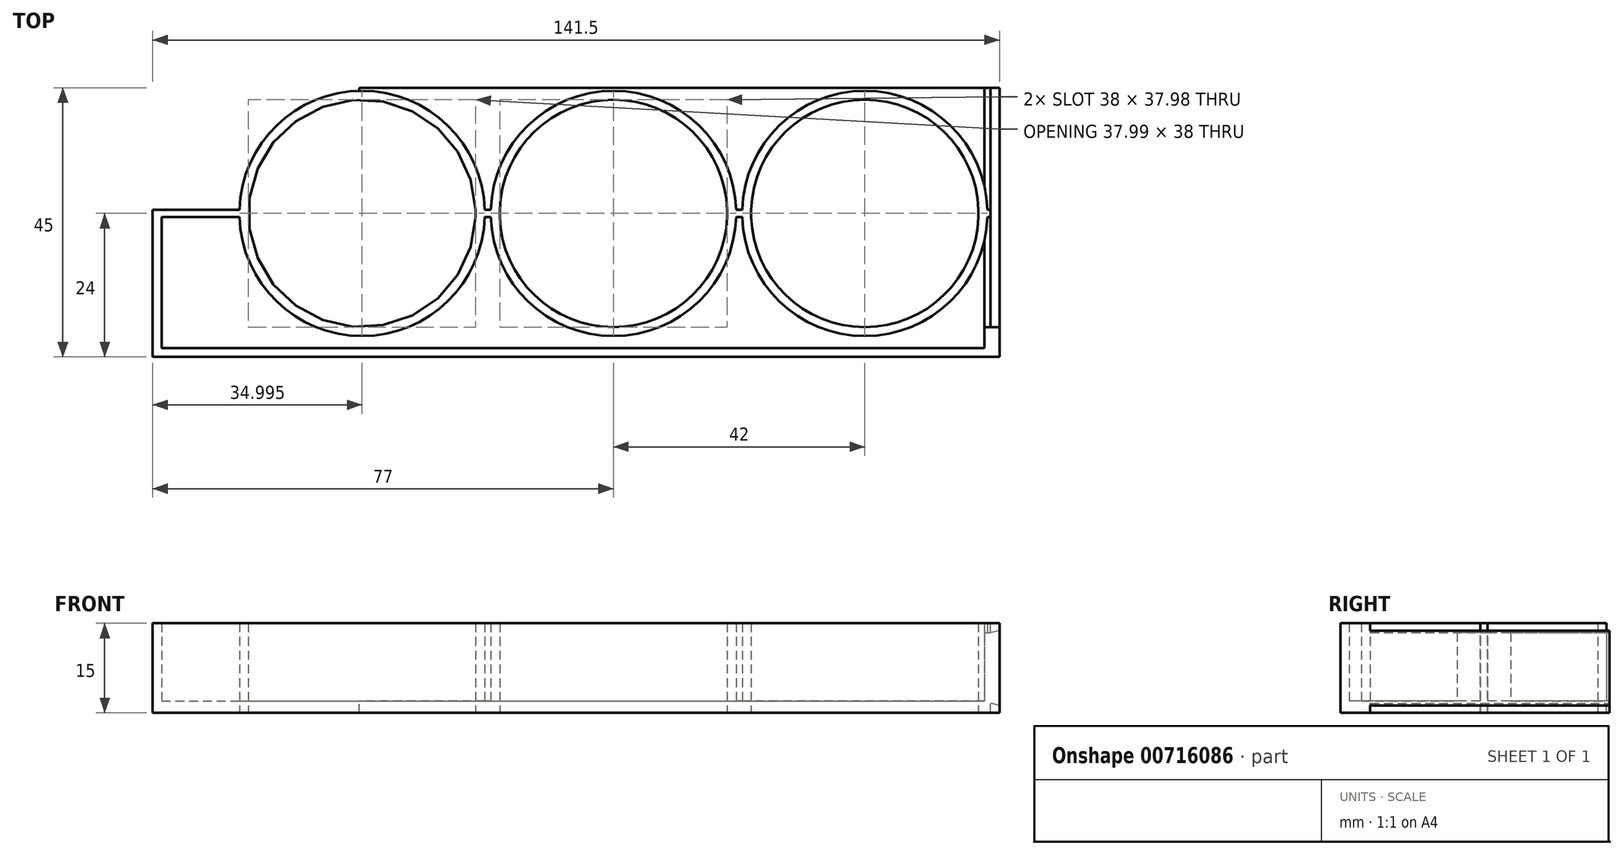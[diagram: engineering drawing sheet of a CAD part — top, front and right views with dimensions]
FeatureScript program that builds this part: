
annotation { "Feature Type Name" : "Feature", "Feature Type Description" : "" }
export const myFeature = defineFeature(function(context is Context, id is Id, definition is map)
    precondition{}
    {
        {
            var Q0;
            Q0=qCreatedBy(makeId("Top.planeOp"),FACE);
            var sketch = newSketch(context, id + "F0", { "sketchPlane" : qUnion([Q0])});
            skCircle(sketch, "E0", {"center": v(-41.38, 6.47) * mm, "radius": 19 * mm});
            skCircle(sketch, "E1.1.0.0", {"center": v(0.62, 6.47) * mm, "radius": 19 * mm});
            skCircle(sketch, "E1.2.0.0", {"center": v(42.62, 6.47) * mm, "radius": 19 * mm});
            skLineSegment(sketch, "E1.direction1", {"start": v(-41.38, 6.47) * mm, "end": v(0.62, 6.47) * mm, "construction": true});
            skLineSegment(sketch, "E2.bottom", {"start": v(-74.88, 27.47) * mm, "end": v(63.62, 27.47) * mm});
            skLineSegment(sketch, "E2.top", {"start": v(-74.88, -16.03) * mm, "end": v(63.62, -16.03) * mm});
            skLineSegment(sketch, "E2.left", {"start": v(-74.88, 27.47) * mm, "end": v(-74.88, -16.03) * mm});
            skLineSegment(sketch, "E2.right", {"start": v(63.62, 27.47) * mm, "end": v(63.62, -16.03) * mm});
            skCircle(sketch, "E3", {"center": v(-41.38, 6.47) * mm, "radius": 20.5 * mm});
            skCircle(sketch, "E4", {"center": v(0.62, 6.47) * mm, "radius": 20.5 * mm});
            skCircle(sketch, "E5", {"center": v(42.62, 6.47) * mm, "radius": 20.5 * mm});
            skLineSegment(sketch, "E6.0", {"start": v(65.12, 27.47) * mm, "end": v(65.12, -17.53) * mm});
            skLineSegment(sketch, "E6.1", {"start": v(-76.38, -17.53) * mm, "end": v(65.12, -17.53) * mm});
            skLineSegment(sketch, "E6.2", {"start": v(-76.38, 27.47) * mm, "end": v(-76.38, -17.53) * mm});
            skLineSegment(sketch, "E7", {"start": v(63.62, 27.47) * mm, "end": v(65.12, 27.47) * mm});
            skLineSegment(sketch, "E8", {"start": v(-76.38, 27.47) * mm, "end": v(-74.88, 27.47) * mm});
            skSolve(sketch);
        }
        {
            var Q0;
            Q0=makeQuery(id+"F0.imprint","IMPRINT",FACE,{"disambiguationData":[TD([[makeQuery(id+"F0.imprint","IMPRINT",EDGE,{"derivedFrom":sQuery(id+"F0.wireOp",EDGE,"E0")}),-1.0]])]});
            var Q1;
            Q1=makeQuery(id+"F0.imprint","IMPRINT",FACE,{"disambiguationData":[TD([[makeQuery(id+"F0.imprint","IMPRINT",EDGE,{"derivedFrom":sQuery(id+"F0.wireOp",EDGE,"E1.1.0.0")}),-1.0]])]});
            var Q2;
            Q2=makeQuery(id+"F0.imprint","IMPRINT",FACE,{"disambiguationData":[TD([[makeQuery(id+"F0.imprint","IMPRINT",EDGE,{"derivedFrom":sQuery(id+"F0.wireOp",EDGE,"E1.2.0.0")}),-1.0]])]});
            var Q3;
            Q3=makeQuery(id+"F0.imprint","IMPRINT",FACE,{"disambiguationData":[TD([[makeQuery(id+"F0.imprint","IMPRINT",EDGE,{"derivedFrom":sQuery(id+"F0.wireOp",EDGE,"E2.top")}),-1.0]])]});
            extrude(context, id + "F1", {"entities" : qUnion([Q0, Q1, Q2, Q3]), "depth" : 15 * mm, "offsetDistance" : 25 * mm});
        }
        {
            var Q0;
            Q0=makeQuery(id+"F0.imprint","IMPRINT",FACE,{"disambiguationData":[TD([[makeQuery(id+"F0.imprint","IMPRINT",EDGE,{"derivedFrom":sQuery(id+"F0.wireOp",EDGE,"E2.bottom")}),-1.0]])]});
            extrude(context, id + "F2", {"entities" : qUnion([Q0]), "depth" : 2 * mm, "offsetDistance" : 25 * mm});
        }
        {
            var Q0;
            Q0=makeQuery(id+"F1.opExtrude","SWEPT_BODY",BODY,{"disambiguationData":[OSD([sQuery(id+"F0.wireOp",EDGE,"E1.1.0.0"),sQuery(id+"F0.wireOp",EDGE,"E4")])]});
            var Q1;
            Q1=makeQuery(id+"F1.opExtrude","SWEPT_BODY",BODY,{"disambiguationData":[OSD([sQuery(id+"F0.wireOp",EDGE,"E1.2.0.0"),sQuery(id+"F0.wireOp",EDGE,"E5")])]});
            var Q2;
            Q2=makeQuery(id+"F1.opExtrude","SWEPT_BODY",BODY,{"disambiguationData":[OSD([sQuery(id+"F0.wireOp",EDGE,"E2.top"),sQuery(id+"F0.wireOp",EDGE,"E2.left"),sQuery(id+"F0.wireOp",EDGE,"E2.right"),sQuery(id+"F0.wireOp",EDGE,"E6.0"),sQuery(id+"F0.wireOp",EDGE,"E6.1"),sQuery(id+"F0.wireOp",EDGE,"E6.2"),sQuery(id+"F0.wireOp",EDGE,"E7"),sQuery(id+"F0.wireOp",EDGE,"E8")])]});
            var Q3;
            Q3=makeQuery(id+"F2.opExtrude","SWEPT_BODY",BODY,{"disambiguationData":[OSD([sQuery(id+"F0.wireOp",EDGE,"E2.bottom"),sQuery(id+"F0.wireOp",EDGE,"E2.top"),sQuery(id+"F0.wireOp",EDGE,"E2.left"),sQuery(id+"F0.wireOp",EDGE,"E2.right"),sQuery(id+"F0.wireOp",EDGE,"E3"),sQuery(id+"F0.wireOp",EDGE,"E4"),sQuery(id+"F0.wireOp",EDGE,"E5")])]});
            var Q4;
            Q4=makeQuery(id+"F1.opExtrude","SWEPT_BODY",BODY,{"disambiguationData":[OSD([sQuery(id+"F0.wireOp",EDGE,"E0"),sQuery(id+"F0.wireOp",EDGE,"E3")])]});
            booleanBodies(context, id + "F3", {"operationType" : BooleanOperationType.UNION, "tools" : qUnion([Q0, Q1, Q2, Q3, Q4])});
        }
        {
            var Q0;
            Q0=makeQuery(id+"F1.opExtrude","SWEPT_BODY",BODY,{"disambiguationData":[OSD([sQuery(id+"F0.wireOp",EDGE,"E1.1.0.0"),sQuery(id+"F0.wireOp",EDGE,"E4")])]});
            var Q1;
            Q1=sQuery(id+"F0.wireOp",VERTEX,"E1.direction1.end");
            var Q2;
            Q2=qCreatedBy(makeId("Origin.pointOp"),VERTEX);
            transform(context, id + "F4", {"entities" : qUnion([Q0]), "transformType" : TransformType.TRANSLATION_ENTITY, "oppositeDirectionEntity" : false, "transformLine" : qUnion([Q1, Q2]), "makeCopy" : false});
        }
        {
            var Q0;
            Q0=makeQuery(id+"F1.opExtrude","SWEPT_FACE",FACE,{"disambiguationData":[OSD([sQuery(id+"F0.wireOp",EDGE,"E6.2")])]});
            var sketch = newSketch(context, id + "F5", { "sketchPlane" : qUnion([Q0])});
            skLineSegment(sketch, "E9.bottom", {"start": v(0.6, 0) * mm, "end": v(-0.6, 0) * mm});
            skLineSegment(sketch, "E9.top", {"start": v(0.6, 15) * mm, "end": v(-0.6, 15) * mm});
            skLineSegment(sketch, "E9.left", {"start": v(0.6, 0) * mm, "end": v(0.6, 15) * mm});
            skLineSegment(sketch, "E9.right", {"start": v(-0.6, 0) * mm, "end": v(-0.6, 15) * mm});
            skSolve(sketch);
        }
        {
            var Q0;
            Q0=makeQuery(id+"F5.imprint","IMPRINT",FACE,{"disambiguationData":[TD([[makeQuery(id+"F5.imprint","IMPRINT",EDGE,{"derivedFrom":sQuery(id+"F5.wireOp",EDGE,"E9.bottom")}),1.0]])]});
            extrude(context, id + "F6", {"entities" : qUnion([Q0]), "operationType" : NewBodyOperationType.ADD, "oppositeDirection" : true, "depth" : 16 * mm, "offsetDistance" : 25 * mm});
        }
        {
            var Q0;
            Q0=makeQuery(id+"F2.opExtrude","CAP_FACE",FACE,{"disambiguationData":[OSD([sQuery(id+"F0.wireOp",EDGE,"E2.bottom"),sQuery(id+"F0.wireOp",EDGE,"E2.top"),sQuery(id+"F0.wireOp",EDGE,"E2.left"),sQuery(id+"F0.wireOp",EDGE,"E2.right"),sQuery(id+"F0.wireOp",EDGE,"E3"),sQuery(id+"F0.wireOp",EDGE,"E4"),sQuery(id+"F0.wireOp",EDGE,"E5")])],"isStart":false});
            var sketch = newSketch(context, id + "F7", { "sketchPlane" : qUnion([Q0])});
            skLineSegment(sketch, "E10", {"start": v(-42.5, 21) * mm, "end": v(-42.5, 20.5) * mm});
            skSolve(sketch);
        }
        {
            var Q0;
            {var subQ7=sQuery(id+"F7.wireOp",EDGE,"E10");Q0=makeQuery(id+"F7.imprint","IMPRINT",FACE,{"disambiguationData":[TD([[makeQuery(id+"F7.imprint","IMPRINT",EDGE,{"derivedFrom":subQ7}),-1.0]])]});}
            extrude(context, id + "F8", {"entities" : qUnion([Q0]), "operationType" : NewBodyOperationType.REMOVE, "endBound" : BoundingType.THROUGH_ALL, "oppositeDirection" : true, "depth" : 25 * mm, "offsetDistance" : 25 * mm});
        }
        {
            var Q0;
            Q0=makeQuery(id+"F6.boolean.opBoolean","MERGE",FACE,{"derivedFrom":[makeQuery(id+"F1.opExtrude","CAP_FACE",FACE,{"disambiguationData":[OSD([sQuery(id+"F0.wireOp",EDGE,"E0"),sQuery(id+"F0.wireOp",EDGE,"E3")])],"isStart":false}),makeQuery(id+"F1.opExtrude","CAP_FACE",FACE,{"disambiguationData":[OSD([sQuery(id+"F0.wireOp",EDGE,"E2.top"),sQuery(id+"F0.wireOp",EDGE,"E2.left"),sQuery(id+"F0.wireOp",EDGE,"E2.right"),sQuery(id+"F0.wireOp",EDGE,"E6.0"),sQuery(id+"F0.wireOp",EDGE,"E6.1"),sQuery(id+"F0.wireOp",EDGE,"E6.2"),sQuery(id+"F0.wireOp",EDGE,"E7"),sQuery(id+"F0.wireOp",EDGE,"E8")])],"isStart":false}),makeQuery(id+"F6.opExtrude","SWEPT_FACE",FACE,{"disambiguationData":[OSD([sQuery(id+"F5.wireOp",EDGE,"E9.top")])]})]});
            var sketch = newSketch(context, id + "F9", { "sketchPlane" : qUnion([Q0])});
            skLineSegment(sketch, "E11", {"start": v(-75.5, 0.6) * mm, "end": v(-77, 0.6) * mm});
            skSolve(sketch);
        }
        {
            var Q0;
            {var subQ0=sQuery(id+"F9.wireOp",EDGE,"E11");Q0=makeQuery(id+"F9.imprint","IMPRINT",FACE,{"disambiguationData":[TD([[makeQuery(id+"F9.imprint","IMPRINT",EDGE,{"derivedFrom":subQ0}),-1.0]])]});}
            extrude(context, id + "F10", {"entities" : qUnion([Q0]), "operationType" : NewBodyOperationType.REMOVE, "endBound" : BoundingType.THROUGH_ALL, "oppositeDirection" : true, "depth" : 25 * mm, "offsetDistance" : 25 * mm});
        }
        {
            var Q0;
            Q0=makeQuery(id+"F1.opExtrude","SWEPT_FACE",FACE,{"disambiguationData":[OSD([sQuery(id+"F0.wireOp",EDGE,"E6.0")])]});
            var sketch = newSketch(context, id + "F11", { "sketchPlane" : qUnion([Q0])});
            skLineSegment(sketch, "E12.bottom", {"start": v(19.8, 0) * mm, "end": v(21, 0) * mm});
            skLineSegment(sketch, "E12.top", {"start": v(19.8, 11) * mm, "end": v(21, 11) * mm});
            skLineSegment(sketch, "E12.left", {"start": v(19.8, 0) * mm, "end": v(19.8, 11) * mm});
            skLineSegment(sketch, "E12.right", {"start": v(21, 0) * mm, "end": v(21, 11) * mm});
            skLineSegment(sketch, "E13.bottom", {"start": v(-0.6, 0) * mm, "end": v(0.6, 0) * mm});
            skLineSegment(sketch, "E13.top", {"start": v(-0.6, 15) * mm, "end": v(0.6, 15) * mm});
            skLineSegment(sketch, "E13.left", {"start": v(-0.6, 0) * mm, "end": v(-0.6, 15) * mm});
            skLineSegment(sketch, "E13.right", {"start": v(0.6, 0) * mm, "end": v(0.6, 15) * mm});
            skSolve(sketch);
        }
        {
            var Q0;
            Q0=makeQuery(id+"F11.imprint","IMPRINT",FACE,{"disambiguationData":[TD([[makeQuery(id+"F11.imprint","IMPRINT",EDGE,{"derivedFrom":sQuery(id+"F11.wireOp",EDGE,"E13.bottom")}),-1.0]])]});
            extrude(context, id + "F12", {"entities" : qUnion([Q0]), "operationType" : NewBodyOperationType.ADD, "oppositeDirection" : true, "depth" : 125 * mm, "offsetDistance" : 25 * mm});
        }
        {
            var Q0;
            {var subQ0=sQuery(id+"F0.wireOp",EDGE,"E6.0");var subQ1=makeQuery(id+"FiQoBUk4rasaOa6_2.boolean.opBoolean","MERGE",FACE,{"derivedFrom":[makeQuery(id+"F1.opExtrude","CAP_FACE",FACE,{"disambiguationData":[OSD([sQuery(id+"F0.wireOp",EDGE,"E1.2.0.0"),sQuery(id+"F0.wireOp",EDGE,"E5")])],"isStart":false}),makeQuery(id+"F6.boolean.opBoolean","MERGE",FACE,{"derivedFrom":[makeQuery(id+"F1.opExtrude","CAP_FACE",FACE,{"disambiguationData":[OSD([sQuery(id+"F0.wireOp",EDGE,"E0"),sQuery(id+"F0.wireOp",EDGE,"E3")])],"isStart":false}),makeQuery(id+"F1.opExtrude","CAP_FACE",FACE,{"disambiguationData":[OSD([sQuery(id+"F0.wireOp",EDGE,"E2.top"),sQuery(id+"F0.wireOp",EDGE,"E2.left"),sQuery(id+"F0.wireOp",EDGE,"E2.right"),subQ0,sQuery(id+"F0.wireOp",EDGE,"E6.1"),sQuery(id+"F0.wireOp",EDGE,"E6.2"),sQuery(id+"F0.wireOp",EDGE,"E7"),sQuery(id+"F0.wireOp",EDGE,"E8")])],"isStart":false}),makeQuery(id+"F6.opExtrude","SWEPT_FACE",FACE,{"disambiguationData":[OSD([sQuery(id+"F5.wireOp",EDGE,"E9.top")])]})]}),makeQuery(id+"FiQoBUk4rasaOa6_2.opExtrude","SWEPT_FACE",FACE,{"disambiguationData":[OSD([subQ0])]})]});Q0=makeQuery(id+"F12.boolean.opBoolean","MERGE",FACE,{"derivedFrom":[makeQuery(id+"F1.opExtrude","CAP_FACE",FACE,{"disambiguationData":[OSD([sQuery(id+"F0.wireOp",EDGE,"E1.1.0.0"),sQuery(id+"F0.wireOp",EDGE,"E4")])],"isStart":false}),makeQuery(id+"FaKzgxXDc0kuBug_2.opFillet","SPLIT",FACE,{"disambiguationData":[OD(0.0)],"derivedFrom":subQ1}),makeQuery(id+"FaKzgxXDc0kuBug_2.opFillet","SPLIT",FACE,{"disambiguationData":[OD(1.0)],"derivedFrom":subQ1}),makeQuery(id+"F12.opExtrude","SWEPT_FACE",FACE,{"disambiguationData":[OSD([sQuery(id+"F11.wireOp",EDGE,"E13.top")])]})]});}
            var sketch = newSketch(context, id + "F13", { "sketchPlane" : qUnion([Q0])});
            skLineSegment(sketch, "E14", {"start": v(-23, -0.6) * mm, "end": v(-23, 0.6) * mm});
            skLineSegment(sketch, "E15", {"start": v(-19, -0.6) * mm, "end": v(-19, 0.6) * mm});
            skLineSegment(sketch, "E16", {"start": v(19, -0.6) * mm, "end": v(19, 0.6) * mm});
            skLineSegment(sketch, "E17", {"start": v(23, -0.6) * mm, "end": v(23, 0.6) * mm});
            skLineSegment(sketch, "E18", {"start": v(61, -0.6) * mm, "end": v(61, 0.6) * mm});
            skSolve(sketch);
        }
        {
            var Q0;
            Q0=makeQuery(id+"F13.imprint","IMPRINT",FACE,{"disambiguationData":[TD([[makeQuery(id+"F13.imprint","IMPRINT",EDGE,{"derivedFrom":sQuery(id+"F13.wireOp",EDGE,"E17")}),-1.0]])]});
            var Q1;
            Q1=makeQuery(id+"F13.imprint","IMPRINT",FACE,{"disambiguationData":[TD([[makeQuery(id+"F13.imprint","IMPRINT",EDGE,{"derivedFrom":sQuery(id+"F13.wireOp",EDGE,"E15")}),-1.0]])]});
            var Q2;
            Q2=makeQuery(id+"F13.imprint","IMPRINT",FACE,{"disambiguationData":[TD([[makeQuery(id+"F13.imprint","IMPRINT",EDGE,{"derivedFrom":sQuery(id+"F13.wireOp",EDGE,"E14")}),1.0]])]});
            extrude(context, id + "F14", {"entities" : qUnion([Q0, Q1, Q2]), "operationType" : NewBodyOperationType.REMOVE, "endBound" : BoundingType.THROUGH_ALL, "oppositeDirection" : true, "depth" : 25 * mm, "offsetDistance" : 25 * mm});
        }
        {
            var Q0;
            {var subQ0=sQuery(id+"F0.wireOp",EDGE,"E7");var subQ1=sQuery(id+"F0.wireOp",EDGE,"E6.0");var subQ5=sQuery(id+"F0.wireOp",EDGE,"E2.right");var subQ8=sQuery(id+"F0.wireOp",EDGE,"E2.bottom");var subQ9=sQuery(id+"F0.wireOp",EDGE,"E8");Q0=makeQuery(id+"FaiT4b11NJjoTD2_2.boolean.opBoolean","MERGE",FACE,{"derivedFrom":[makeQuery(id+"F8.boolean.opBoolean","SPLIT",FACE,{"disambiguationData":[TD([makeQuery(id+"F1.opExtrude","SWEPT_FACE",FACE,{"disambiguationData":[OSD([subQ5])]})])],"derivedFrom":makeQuery(id+"F3.opBoolean","MERGE",FACE,{"derivedFrom":[makeQuery(id+"F1.opExtrude","SWEPT_FACE",FACE,{"disambiguationData":[OSD([subQ0])]}),makeQuery(id+"F1.opExtrude","SWEPT_FACE",FACE,{"disambiguationData":[OSD([subQ9])]}),makeQuery(id+"F2.opExtrude","SWEPT_FACE",FACE,{"disambiguationData":[OSD([subQ8])]})]})}),makeQuery(id+"FaiT4b11NJjoTD2_2.opExtrude","SWEPT_FACE",FACE,{"disambiguationData":[OSD([subQ1,subQ0])]})]});}
            var sketch = newSketch(context, id + "F15", { "sketchPlane" : qUnion([Q0])});
            skLineSegment(sketch, "E19", {"start": v(-65.5, 7.5) * mm, "end": v(-63.53, 7.5) * mm});
            skLineSegment(sketch, "E20.bottom", {"start": v(-65.5, 15) * mm, "end": v(-63, 15) * mm});
            skLineSegment(sketch, "E20.left", {"start": v(-65.5, 15) * mm, "end": v(-65.5, 14) * mm});
            skLineSegment(sketch, "E20.right", {"start": v(-63, 15) * mm, "end": v(-63, 14) * mm});
            skLineSegment(sketch, "E21", {"start": v(-65.5, 14) * mm, "end": v(-63, 13.4) * mm});
            skLineSegment(sketch, "E22.MirrorCS", {"start": v(-65.5, 0) * mm, "end": v(-63, 0) * mm});
            skLineSegment(sketch, "E23.MirrorCS", {"start": v(-65.5, 0) * mm, "end": v(-65.5, 1) * mm});
            skLineSegment(sketch, "E24.MirrorCS", {"start": v(-65.5, 1) * mm, "end": v(-63, 1.6) * mm});
            skLineSegment(sketch, "E25.MirrorCS", {"start": v(-63, 0) * mm, "end": v(-63, 1.6) * mm});
            skPoint(sketch, "E26.orphan", {"position": v(-63, 1) * mm});
            skSolve(sketch);
        }
        {
            var Q0;
            {var subQ0=sQuery(id+"F15.wireOp",EDGE,"E20.top");Q0=makeQuery(id+"F15.imprint","IMPRINT",FACE,{"disambiguationData":[TD([[makeQuery(id+"F15.imprint","IMPRINT",EDGE,{"derivedFrom":subQ0}),-1.0]])]});}
            var Q1;
            Q1=makeQuery(id+"F15.imprint","IMPRINT",FACE,{"disambiguationData":[TD([[makeQuery(id+"F15.imprint","IMPRINT",EDGE,{"derivedFrom":sQuery(id+"F15.wireOp",EDGE,"E20.bottom")}),1.0]])]});
            var Q2;
            Q2=makeQuery(id+"F15.imprint","IMPRINT",FACE,{"disambiguationData":[TD([[makeQuery(id+"F15.imprint","IMPRINT",EDGE,{"derivedFrom":sQuery(id+"F15.wireOp",EDGE,"E22.MirrorCS")}),-1.0]])]});
            extrude(context, id + "F16", {"entities" : qUnion([Q0, Q1, Q2]), "operationType" : NewBodyOperationType.REMOVE, "oppositeDirection" : true, "depth" : 40 * mm, "offsetDistance" : 25 * mm});
        }
        {
            var Q0;
            {var subQ3=sQuery(id+"F0.wireOp",EDGE,"E2.right");var subQ8=sQuery(id+"F0.wireOp",EDGE,"E7");Q0=makeQuery(id+"F12.boolean.opBoolean","SPLIT",FACE,{"disambiguationData":[TD([makeQuery(id+"F1.opExtrude","SWEPT_FACE",FACE,{"disambiguationData":[OSD([subQ8])]})])],"derivedFrom":makeQuery(id+"F1.opExtrude","SWEPT_FACE",FACE,{"disambiguationData":[OSD([subQ3])]})});}
            var sketch = newSketch(context, id + "F17", { "sketchPlane" : qUnion([Q0])});
            skSolve(sketch);
        }
        {
            var Q0;
            {var subQ0=sQuery(id+"F0.wireOp",EDGE,"E2.bottom");var subQ4=sQuery(id+"F0.wireOp",EDGE,"E7");var subQ6=sQuery(id+"F0.wireOp",EDGE,"E2.right");Q0=makeQuery(id+"F17.imprint","IMPRINT",FACE,{"disambiguationData":[TD([[makeQuery(id+"F17.imprint","IMPRINT",EDGE,{"derivedFrom":makeQuery(id+"F1.opExtrude","SWEPT_EDGE",EDGE,{"disambiguationData":[OSD([subQ0,subQ6,subQ4])]})}),1.0]])]});}
            var Q1;
            {var subQ0=sQuery(id+"F0.wireOp",EDGE,"E2.top");var subQ4=sQuery(id+"F0.wireOp",EDGE,"E2.right");Q1=makeQuery(id+"F12.boolean.opBoolean","SPLIT",FACE,{"disambiguationData":[TD([makeQuery(id+"F1.opExtrude","SWEPT_FACE",FACE,{"disambiguationData":[OSD([subQ0])]})])],"derivedFrom":makeQuery(id+"F1.opExtrude","SWEPT_FACE",FACE,{"disambiguationData":[OSD([subQ4])]})});}
            extrude(context, id + "F18", {"entities" : qUnion([Q0, Q1]), "operationType" : NewBodyOperationType.ADD, "depth" : 1 * mm, "offsetDistance" : 25 * mm});
        }
    });
